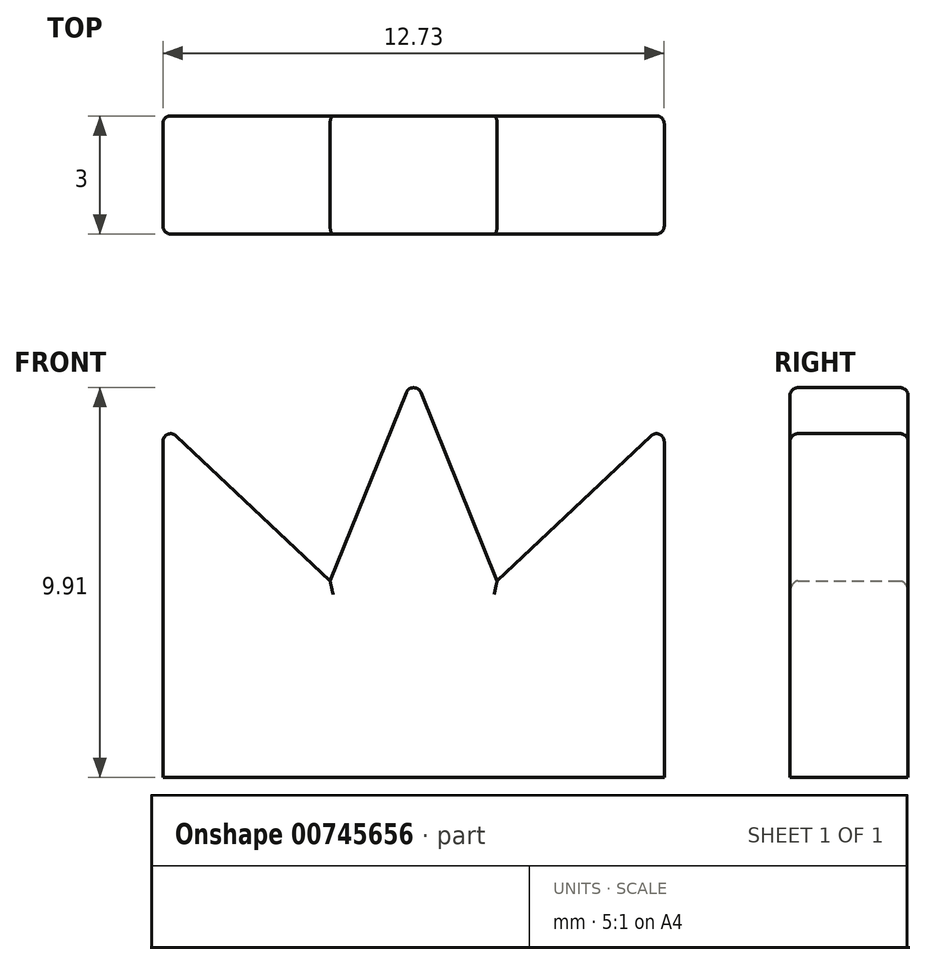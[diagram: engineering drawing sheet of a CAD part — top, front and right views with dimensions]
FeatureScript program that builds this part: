
annotation { "Feature Type Name" : "Feature", "Feature Type Description" : "" }
export const myFeature = defineFeature(function(context is Context, id is Id, definition is map)
    precondition{}
    {
        {
            var Q0;
            Q0=qCreatedBy(makeId("Front.planeOp"),FACE);
            var sketch = newSketch(context, id + "F0", { "sketchPlane" : qUnion([Q0])});
            skLineSegment(sketch, "E0", {"start": v(0, 0) * mm, "end": v(12.73, 0) * mm});
            skLineSegment(sketch, "E1", {"start": v(12.73, 0) * mm, "end": v(12.73, 5) * mm});
            skLineSegment(sketch, "E2", {"start": v(0, 0) * mm, "end": v(0, 5) * mm});
            skLineSegment(sketch, "E3", {"start": v(0, 5) * mm, "end": v(0, 6.5) * mm});
            skLineSegment(sketch, "E4", {"start": v(0, 6.5) * mm, "end": v(0, 9) * mm});
            skLineSegment(sketch, "E5", {"start": v(0, 9) * mm, "end": v(4.25, 5) * mm});
            skLineSegment(sketch, "E6", {"start": v(12.73, 5) * mm, "end": v(12.73, 9) * mm});
            skLineSegment(sketch, "E7", {"start": v(12.73, 9) * mm, "end": v(8.49, 5) * mm});
            skLineSegment(sketch, "E8", {"start": v(6.37, 10.24) * mm, "end": v(8.5, 5) * mm});
            skLineSegment(sketch, "E9", {"start": v(6.37, 10.24) * mm, "end": v(4.24, 5) * mm});
            skPoint(sketch, "E10.end.orphan", {"position": v(2.12, 5) * mm});
            skPoint(sketch, "E11.start.orphan", {"position": v(6.37, 5) * mm});
            skSolve(sketch);
        }
        {
            var Q0;
            Q0=makeQuery(id+"F0.imprint","IMPRINT",FACE,{"disambiguationData":[TD([[makeQuery(id+"F0.imprint","IMPRINT",EDGE,{"derivedFrom":sQuery(id+"F0.wireOp",EDGE,"E0")}),1.0]])]});
            extrude(context, id + "F1", {"entities" : qUnion([Q0]), "depth" : 3 * mm, "offsetDistance" : 25 * mm});
        }
        {
            var Q0;
            Q0=makeQuery(id+"F1.opExtrude","SWEPT_EDGE",EDGE,{"disambiguationData":[OSD([sQuery(id+"F0.wireOp",EDGE,"E4"),sQuery(id+"F0.wireOp",EDGE,"E5")])]});
            var Q1;
            Q1=makeQuery(id+"F1.opExtrude","SWEPT_EDGE",EDGE,{"disambiguationData":[OSD([sQuery(id+"F0.wireOp",EDGE,"E8"),sQuery(id+"F0.wireOp",EDGE,"E9")])]});
            var Q2;
            Q2=makeQuery(id+"F1.opExtrude","CAP_EDGE",EDGE,{"disambiguationData":[OSD([sQuery(id+"F0.wireOp",EDGE,"E1"),sQuery(id+"F0.wireOp",EDGE,"E6")])],"isStart":true});
            var Q3;
            Q3=makeQuery(id+"F1.opExtrude","CAP_EDGE",EDGE,{"disambiguationData":[OSD([sQuery(id+"F0.wireOp",EDGE,"E8")])],"isStart":false});
            var Q4;
            Q4=makeQuery(id+"F1.opExtrude","CAP_EDGE",EDGE,{"disambiguationData":[OSD([sQuery(id+"F0.wireOp",EDGE,"E9")])],"isStart":false});
            var Q5;
            Q5=makeQuery(id+"F1.opExtrude","CAP_EDGE",EDGE,{"disambiguationData":[OSD([sQuery(id+"F0.wireOp",EDGE,"E5")])],"isStart":false});
            var Q6;
            Q6=makeQuery(id+"F1.opExtrude","CAP_EDGE",EDGE,{"disambiguationData":[OSD([sQuery(id+"F0.wireOp",EDGE,"E7")])],"isStart":false});
            var Q7;
            Q7=makeQuery(id+"F1.opExtrude","CAP_EDGE",EDGE,{"disambiguationData":[OSD([sQuery(id+"F0.wireOp",EDGE,"E7")])],"isStart":true});
            var Q8;
            Q8=makeQuery(id+"F1.opExtrude","CAP_EDGE",EDGE,{"disambiguationData":[OSD([sQuery(id+"F0.wireOp",EDGE,"E8")])],"isStart":true});
            var Q9;
            Q9=makeQuery(id+"F1.opExtrude","CAP_EDGE",EDGE,{"disambiguationData":[OSD([sQuery(id+"F0.wireOp",EDGE,"E9")])],"isStart":true});
            var Q10;
            Q10=makeQuery(id+"F1.opExtrude","CAP_EDGE",EDGE,{"disambiguationData":[OSD([sQuery(id+"F0.wireOp",EDGE,"E5")])],"isStart":true});
            var Q11;
            Q11=makeQuery(id+"F1.opExtrude","CAP_EDGE",EDGE,{"disambiguationData":[OSD([sQuery(id+"F0.wireOp",EDGE,"E2"),sQuery(id+"F0.wireOp",EDGE,"E3"),sQuery(id+"F0.wireOp",EDGE,"E4")])],"isStart":true});
            var Q12;
            Q12=makeQuery(id+"F1.opExtrude","CAP_EDGE",EDGE,{"disambiguationData":[OSD([sQuery(id+"F0.wireOp",EDGE,"E1"),sQuery(id+"F0.wireOp",EDGE,"E6")])],"isStart":false});
            var Q13;
            Q13=makeQuery(id+"F1.opExtrude","CAP_EDGE",EDGE,{"disambiguationData":[OSD([sQuery(id+"F0.wireOp",EDGE,"E2"),sQuery(id+"F0.wireOp",EDGE,"E3"),sQuery(id+"F0.wireOp",EDGE,"E4")])],"isStart":false});
            var Q14;
            Q14=makeQuery(id+"F1.opExtrude","SWEPT_EDGE",EDGE,{"disambiguationData":[OSD([sQuery(id+"F0.wireOp",EDGE,"E6"),sQuery(id+"F0.wireOp",EDGE,"E7")])]});
            fillet(context, id + "F2", {"entities" : qUnion([Q0, Q1, Q2, Q3, Q4, Q5, Q6, Q7, Q8, Q9, Q10, Q11, Q12, Q13, Q14]), "radius" : 0.2 * mm, "tangentPropagation" : true, "allowEdgeOverflow" : false});
        }
    });
